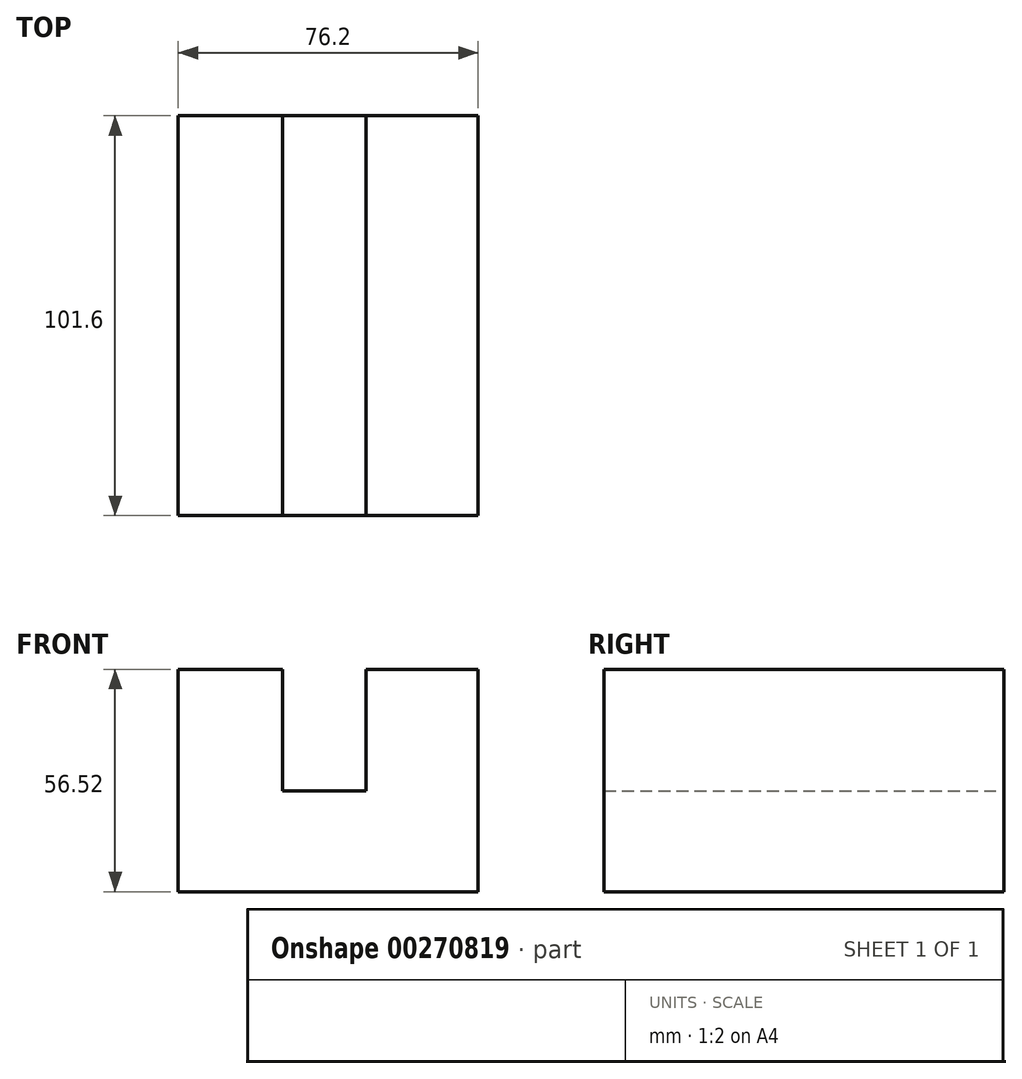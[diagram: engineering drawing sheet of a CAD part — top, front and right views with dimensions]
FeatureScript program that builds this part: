
annotation { "Feature Type Name" : "Feature", "Feature Type Description" : "" }
export const myFeature = defineFeature(function(context is Context, id is Id, definition is map)
    precondition{}
    {
        {
            var Q0;
            Q0=qCreatedBy(makeId("Front.planeOp"),FACE);
            var sketch = newSketch(context, id + "F0", { "sketchPlane" : qUnion([Q0])});
            skLineSegment(sketch, "E0", {"start": v(0, 0) * mm, "end": v(-76.2, 0) * mm});
            skLineSegment(sketch, "E1", {"start": v(-76.2, 0) * mm, "end": v(-76.2, 50.8) * mm});
            skLineSegment(sketch, "E2", {"start": v(-76.2, 50.8) * mm, "end": v(-76.2, 56.52) * mm});
            skLineSegment(sketch, "E3", {"start": v(-76.2, 56.52) * mm, "end": v(-49.65, 56.52) * mm});
            skLineSegment(sketch, "E4", {"start": v(-49.65, 56.52) * mm, "end": v(-49.65, 25.59) * mm});
            skLineSegment(sketch, "E5", {"start": v(-49.65, 25.59) * mm, "end": v(-28.45, 25.59) * mm});
            skLineSegment(sketch, "E6", {"start": v(-28.45, 25.59) * mm, "end": v(-28.45, 56.52) * mm});
            skLineSegment(sketch, "E7", {"start": v(-28.45, 56.52) * mm, "end": v(0, 56.52) * mm});
            skLineSegment(sketch, "E8", {"start": v(0, 56.52) * mm, "end": v(0, 0) * mm});
            skSolve(sketch);
        }
        {
            var Q0;
            Q0 = qSketchRegion(id + "F0", true);
            extrude(context, id + "F1", {"entities" : qUnion([Q0]), "depth" : 101.6 * mm});
        }
    });
